# Revit family: 7-MISC--CADS-7-MISC--CADS-43-6-bed-kit-xl-4-REVIT_Versatex-Generic-Model-6-bed-kit-xl
name_source: partatom
category: Generic Models
units: mm (PartAtom-declared; Revit-internal decimal feet)

## family parameters
Always vertical = Yes
Can host rebar = No
Cut with Voids When Loaded = No
Maintain Annotation Orientation = No
Part Type = Normal
Room Calculation Point = No
Round Connector Dimension = Use Diameter
Shared = No
Work Plane-Based = No

## types (1)
- 7-MISC--CADS-7-MISC--CADS-43-6-bed-kit-xl-4-REVIT_Versatex-Generic-Model-6-bed-kit-xl
    Default Elevation = 0' - 0"
    Description = BED MOULD XL KIT FOR 6" ACCENT WRAP
    Inside Width = 0' - 7 3/4"
    Literature = https://versatex.com
    Manufacturer = Versatex
    Manufacturer Fax = 724-857-1171
    Manufacturer Website = https://versatex.com
    Material = Versatex PVC - Smooth
    Message Manufacturer = https://versatex.com
    Model = VM6"TRIMKITBEDXL
    Sales Information = https://versatex.com
    Specification = https://www.arcat.com
    URL = https://versatex.com
    Warranty = https://versatex.com

## geometry (parser evidence)
native form markers: Blend x2, Sweep x2
no freeform markers — native parametric forms only
